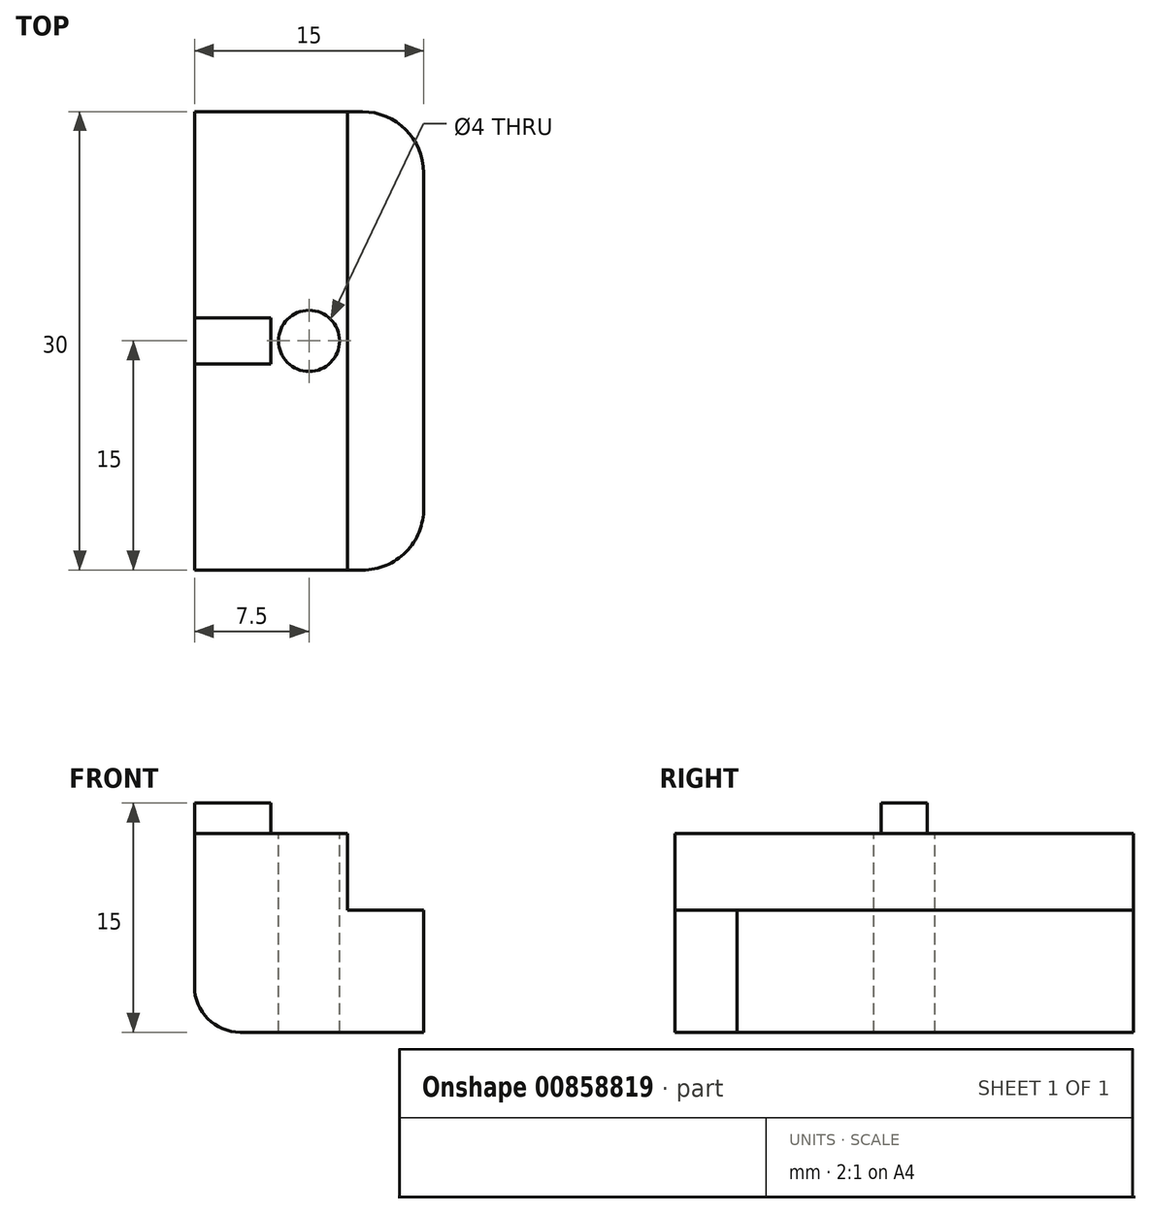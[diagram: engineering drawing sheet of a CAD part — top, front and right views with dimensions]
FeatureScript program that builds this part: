
annotation { "Feature Type Name" : "Feature", "Feature Type Description" : "" }
export const myFeature = defineFeature(function(context is Context, id is Id, definition is map)
    precondition{}
    {
        {
            var Q0;
            Q0=qCreatedBy(makeId("Top.planeOp"),FACE);
            var sketch = newSketch(context, id + "F0", { "sketchPlane" : qUnion([Q0])});
            skLineSegment(sketch, "E0.bottom", {"start": v(0, 0) * mm, "end": v(-11, 0) * mm});
            skLineSegment(sketch, "E0.top", {"start": v(0, 30) * mm, "end": v(-11, 30) * mm});
            skLineSegment(sketch, "E0.right", {"start": v(-11, 0) * mm, "end": v(-11, 30) * mm});
            skArc(sketch, "E1", {"start": v(0, 30) * mm, "mid": v(2.83, 28.83) * mm, "end": v(4, 26) * mm});
            skArc(sketch, "E2", {"start": v(0, 0) * mm, "mid": v(2.84, 1.19) * mm, "end": v(4, 4.04) * mm});
            skLineSegment(sketch, "E3", {"start": v(4, 26) * mm, "end": v(4, 4.04) * mm});
            skSolve(sketch);
        }
        {
            var Q0;
            Q0=makeQuery(id+"F0.imprint","IMPRINT",FACE,{"disambiguationData":[TD([[makeQuery(id+"F0.imprint","IMPRINT",EDGE,{"derivedFrom":sQuery(id+"F0.wireOp",EDGE,"E0.bottom")}),-1.0]])]});
            extrude(context, id + "F1", {"entities" : qUnion([Q0]), "depth" : 8 * mm, "offsetDistance" : 25 * mm});
        }
        {
            var Q0;
            Q0=makeQuery(id+"F1.opExtrude","CAP_FACE",FACE,{"disambiguationData":[OSD([sQuery(id+"F0.wireOp",EDGE,"E0.bottom"),sQuery(id+"F0.wireOp",EDGE,"E0.top"),sQuery(id+"F0.wireOp",EDGE,"E0.right"),sQuery(id+"F0.wireOp",EDGE,"E1"),sQuery(id+"F0.wireOp",EDGE,"E2"),sQuery(id+"F0.wireOp",EDGE,"E3")])],"isStart":false});
            var sketch = newSketch(context, id + "F2", { "sketchPlane" : qUnion([Q0])});
            skLineSegment(sketch, "E4.bottom", {"start": v(-11, 30) * mm, "end": v(-1, 30) * mm});
            skLineSegment(sketch, "E4.top", {"start": v(-11, 0) * mm, "end": v(-1, 0) * mm});
            skLineSegment(sketch, "E4.left", {"start": v(-11, 30) * mm, "end": v(-11, 0) * mm});
            skLineSegment(sketch, "E4.right", {"start": v(-1, 30) * mm, "end": v(-1, 0) * mm});
            skSolve(sketch);
        }
        {
            var Q0;
            Q0=makeQuery(id+"F2.imprint","IMPRINT",FACE,{"disambiguationData":[TD([[makeQuery(id+"F2.imprint","IMPRINT",EDGE,{"derivedFrom":sQuery(id+"F2.wireOp",EDGE,"E4.bottom")}),1.0]])]});
            extrude(context, id + "F3", {"entities" : qUnion([Q0]), "operationType" : NewBodyOperationType.ADD, "depth" : 5 * mm, "offsetDistance" : 25 * mm});
        }
        {
            var Q0;
            Q0=makeQuery(id+"F3.opExtrude","CAP_FACE",FACE,{"disambiguationData":[OSD([sQuery(id+"F2.wireOp",EDGE,"E4.bottom"),sQuery(id+"F2.wireOp",EDGE,"E4.top"),sQuery(id+"F2.wireOp",EDGE,"E4.left"),sQuery(id+"F2.wireOp",EDGE,"E4.right")])],"isStart":false});
            var sketch = newSketch(context, id + "F4", { "sketchPlane" : qUnion([Q0])});
            skLineSegment(sketch, "E5.top", {"start": v(-11, 16.5) * mm, "end": v(-6, 16.5) * mm});
            skLineSegment(sketch, "E5.left", {"start": v(-11, 15) * mm, "end": v(-11, 16.5) * mm});
            skLineSegment(sketch, "E5.right", {"start": v(-6, 15) * mm, "end": v(-6, 16.5) * mm});
            skLineSegment(sketch, "E6.top", {"start": v(-6, 13.5) * mm, "end": v(-11, 13.5) * mm});
            skLineSegment(sketch, "E6.left", {"start": v(-6, 15) * mm, "end": v(-6, 13.5) * mm});
            skLineSegment(sketch, "E6.right", {"start": v(-11, 15) * mm, "end": v(-11, 13.5) * mm});
            skCircle(sketch, "E7", {"center": v(-3.5, 15) * mm, "radius": 2 * mm});
            skSolve(sketch);
        }
        {
            var Q0;
            Q0=makeQuery(id+"F4.imprint","IMPRINT",FACE,{"disambiguationData":[TD([[makeQuery(id+"F4.imprint","IMPRINT",EDGE,{"derivedFrom":sQuery(id+"F4.wireOp",EDGE,"E7")}),1.0]])]});
            var Q1;
            Q1=makeQuery(id+"F3.opExtrude","CAP_FACE",FACE,{"disambiguationData":[OSD([sQuery(id+"F2.wireOp",EDGE,"E4.bottom"),sQuery(id+"F2.wireOp",EDGE,"E4.top"),sQuery(id+"F2.wireOp",EDGE,"E4.left"),sQuery(id+"F2.wireOp",EDGE,"E4.right")])],"isStart":false});
            extrude(context, id + "F5", {"entities" : qUnion([Q0]), "operationType" : NewBodyOperationType.REMOVE, "oppositeDirection" : true, "depth" : 13.9 * mm, "endBoundEntityFace" : qUnion([Q1]), "offsetDistance" : 25 * mm});
        }
        {
            var Q0;
            Q0=makeQuery(id+"F4.imprint","IMPRINT",FACE,{"disambiguationData":[TD([[makeQuery(id+"F4.imprint","IMPRINT",EDGE,{"derivedFrom":sQuery(id+"F4.wireOp",EDGE,"E5.top")}),-1.0]])]});
            extrude(context, id + "F6", {"entities" : qUnion([Q0]), "operationType" : NewBodyOperationType.ADD, "depth" : 2 * mm, "offsetDistance" : 25 * mm});
        }
        {
            var Q0;
            Q0=makeQuery(id+"F1.opExtrude","CAP_EDGE",EDGE,{"disambiguationData":[OSD([sQuery(id+"F0.wireOp",EDGE,"E0.right")])],"isStart":true});
            fillet(context, id + "F7", {"entities" : qUnion([Q0]), "radius" : 3 * mm, "tangentPropagation" : true, "allowEdgeOverflow" : false});
        }
    });
